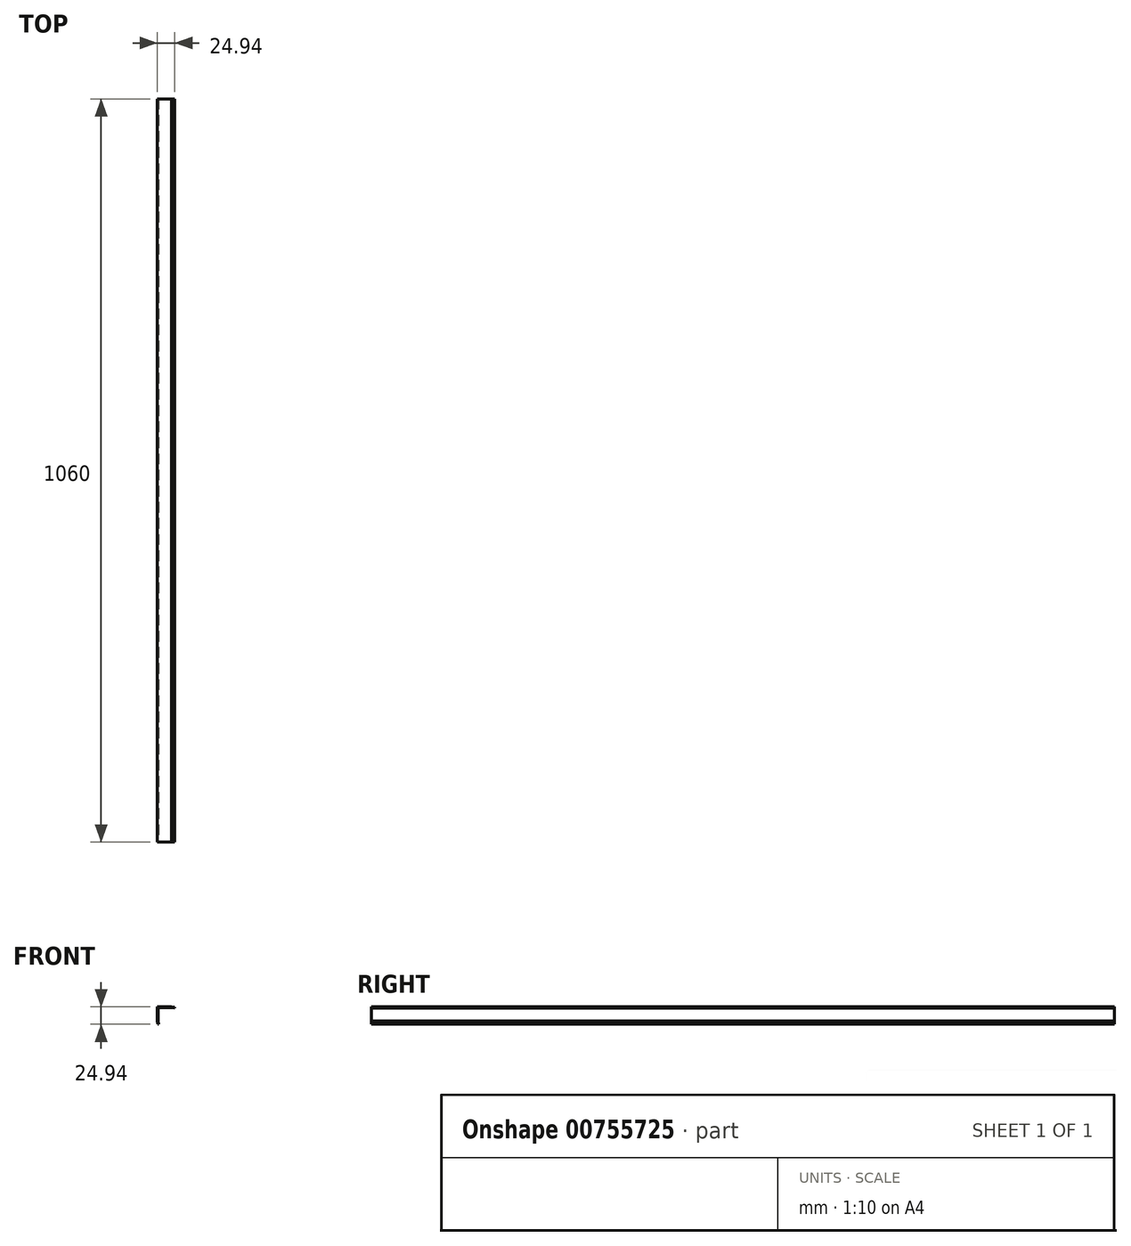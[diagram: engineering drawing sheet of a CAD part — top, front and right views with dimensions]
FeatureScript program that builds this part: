
annotation { "Feature Type Name" : "Feature", "Feature Type Description" : "" }
export const myFeature = defineFeature(function(context is Context, id is Id, definition is map)
    precondition{}
    {
        {
            assignVariable(context, id + "F0", {"name" : "l", "anyValue" : 1060});
        }
        {
            var Q0;
            Q0=qCreatedBy(makeId("Top.planeOp"),FACE);
            var sketch = newSketch(context, id + "F1", { "sketchPlane" : qUnion([Q0])});
            skLineSegment(sketch, "E0.bottom", {"start": v(0, 0) * mm, "end": v(20, 0) * mm});
            skLineSegment(sketch, "E0.top", {"start": v(0, 1) * mm, "end": v(20, 1) * mm});
            skLineSegment(sketch, "E0.left", {"start": v(0, 0) * mm, "end": v(0, 1) * mm});
            skLineSegment(sketch, "E0.right", {"start": v(20, 0) * mm, "end": v(20, 1) * mm});
            skLineSegment(sketch, "E1.bottom", {"start": v(1, 0) * mm, "end": v(1, 20) * mm});
            skLineSegment(sketch, "E1.top", {"start": v(0, 0) * mm, "end": v(0, 20) * mm});
            skLineSegment(sketch, "E1.left", {"start": v(1, 0) * mm, "end": v(0, 0) * mm});
            skLineSegment(sketch, "E1.right", {"start": v(1, 20) * mm, "end": v(0, 20) * mm});
            skLineSegment(sketch, "E2", {"start": v(20, 0) * mm, "end": v(26, 0) * mm, "construction": true});
            skLineSegment(sketch, "E3", {"start": v(20, 0) * mm, "end": v(24.94, 0.8) * mm});
            skLineSegment(sketch, "E4", {"start": v(20, 1) * mm, "end": v(24.92, 1.87) * mm});
            skLineSegment(sketch, "E5", {"start": v(24.94, 0.8) * mm, "end": v(24.92, 1.87) * mm});
            skLineSegment(sketch, "E6", {"start": v(0, 0) * mm, "end": v(25.41, 25.41) * mm, "construction": true});
            skLineSegment(sketch, "E7.MirrorCS", {"start": v(1, 20) * mm, "end": v(1.87, 24.92) * mm});
            skLineSegment(sketch, "E8.MirrorCS", {"start": v(0.8, 24.94) * mm, "end": v(1.87, 24.92) * mm});
            skLineSegment(sketch, "E9.MirrorCS", {"start": v(0, 20) * mm, "end": v(0.8, 24.94) * mm});
            skSolve(sketch);
        }
        {
            var Q0;
            {var subQ5=sQuery(id+"F1.wireOp",EDGE,"E1.right");Q0=makeQuery(id+"F1.imprint","IMPRINT",FACE,{"disambiguationData":[TD([[makeQuery(id+"F1.imprint","IMPRINT",EDGE,{"derivedFrom":subQ5}),1.0]])]});}
            var Q1;
            {var subQ5=sQuery(id+"F1.wireOp",EDGE,"E1.left");Q1=makeQuery(id+"F1.imprint","IMPRINT",FACE,{"disambiguationData":[TD([[makeQuery(id+"F1.imprint","IMPRINT",EDGE,{"derivedFrom":subQ5}),-1.0]])]});}
            var Q2;
            {var subQ0=sQuery(id+"F1.wireOp",EDGE,"E0.bottom");Q2=makeQuery(id+"F1.imprint","IMPRINT",FACE,{"disambiguationData":[TD([[makeQuery(id+"F1.imprint","IMPRINT",EDGE,{"derivedFrom":subQ0}),1.0]])]});}
            extrude(context, id + "F2", {"entities" : qUnion([Q0, Q1, Q2]), "depth" : (getVariable(context, 'l')) * mm, "offsetDistance" : 25 * mm});
        }
        {
            var Q0;
            Q0 = qSketchRegion(id + "F1", true);
            extrude(context, id + "F3", {"entities" : qUnion([Q0]), "operationType" : NewBodyOperationType.ADD, "depth" : 1060 * mm, "offsetDistance" : 25 * mm});
        }
        {
            var Q0;
            Q0=makeQuery(id+"F2.opExtrude","SWEPT_BODY",BODY,{"disambiguationData":[OSD([sQuery(id+"F1.wireOp",EDGE,"E0.bottom"),sQuery(id+"F1.wireOp",EDGE,"E0.top"),sQuery(id+"F1.wireOp",EDGE,"E0.right"),sQuery(id+"F1.wireOp",EDGE,"E1.bottom"),sQuery(id+"F1.wireOp",EDGE,"E1.top"),sQuery(id+"F1.wireOp",EDGE,"E1.left"),sQuery(id+"F1.wireOp",EDGE,"E1.right")])]});
            var Q1;
            Q1=makeQuery(id+"F2.opExtrude","CAP_EDGE",EDGE,{"disambiguationData":[OSD([sQuery(id+"F1.wireOp",EDGE,"E0.bottom"),sQuery(id+"F1.wireOp",EDGE,"E1.left")])],"isStart":true});
            transform(context, id + "F4", {"entities" : qUnion([Q0]), "transformType" : TransformType.ROTATION, "transformAxis" : qUnion([Q1]), "angle" : 90 * degree, "oppositeDirection" : true, "makeCopy" : false});
        }
    });
